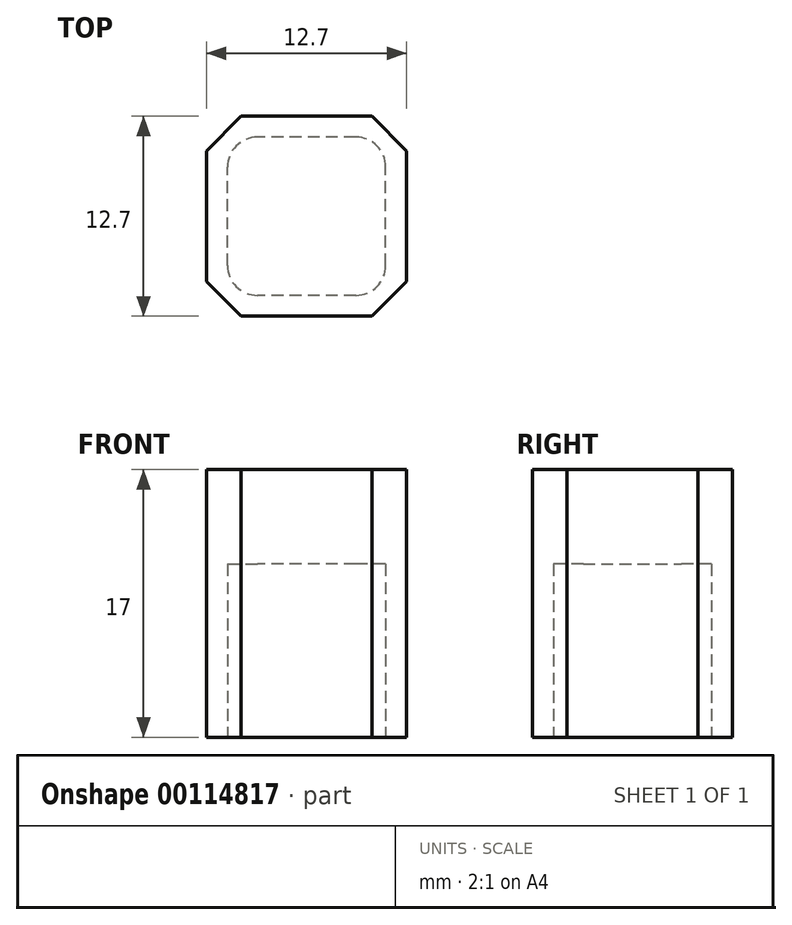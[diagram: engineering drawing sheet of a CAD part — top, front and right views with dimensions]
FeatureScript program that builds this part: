
annotation { "Feature Type Name" : "Feature", "Feature Type Description" : "" }
export const myFeature = defineFeature(function(context is Context, id is Id, definition is map)
    precondition{}
    {
        {
            var Q0;
            Q0=qCreatedBy(makeId("Top.planeOp"),FACE);
            var sketch = newSketch(context, id + "F0", { "sketchPlane" : qUnion([Q0])});
            skLineSegment(sketch, "E0.bottom", {"start": v(-30.85, -32.42) * mm, "end": v(-18.15, -32.42) * mm});
            skLineSegment(sketch, "E0.top", {"start": v(-30.85, -19.72) * mm, "end": v(-18.15, -19.72) * mm});
            skLineSegment(sketch, "E0.left", {"start": v(-30.85, -32.42) * mm, "end": v(-30.85, -19.72) * mm});
            skLineSegment(sketch, "E0.right", {"start": v(-18.15, -32.42) * mm, "end": v(-18.15, -19.72) * mm});
            skLineSegment(sketch, "E1", {"start": v(-18.15, -32.42) * mm, "end": v(-30.85, -19.72) * mm, "construction": true});
            skLineSegment(sketch, "E2", {"start": v(-30.85, -32.42) * mm, "end": v(-18.15, -19.72) * mm, "construction": true});
            skLineSegment(sketch, "E3", {"start": v(-24.5, -26.07) * mm, "end": v(-19.47, -26.07) * mm, "construction": true});
            skPoint(sketch, "E3.endSnap0", {"position": v(-24.5, -26.07) * mm});
            skLineSegment(sketch, "E4", {"start": v(-19.47, -26.07) * mm, "end": v(-19.47, -31.1) * mm, "construction": true});
            skLineSegment(sketch, "E5.bottom", {"start": v(-19.47, -31.1) * mm, "end": v(-29.52, -31.1) * mm});
            skLineSegment(sketch, "E5.top", {"start": v(-19.47, -21.05) * mm, "end": v(-29.52, -21.05) * mm});
            skLineSegment(sketch, "E5.left", {"start": v(-19.47, -31.1) * mm, "end": v(-19.47, -21.05) * mm});
            skLineSegment(sketch, "E5.right", {"start": v(-29.52, -31.1) * mm, "end": v(-29.52, -21.05) * mm});
            skSolve(sketch);
        }
        {
            var Q0;
            Q0 = qSketchRegion(id + "F0", true);
            extrude(context, id + "F1", {"entities" : qUnion([Q0]), "depth" : 17 * mm});
        }
        {
            var Q0;
            Q0=makeQuery(id+"F0.imprint","IMPRINT",FACE,{"disambiguationData":[TD([[makeQuery(id+"F0.imprint","IMPRINT",EDGE,{"derivedFrom":sQuery(id+"F0.wireOp",EDGE,"E5.bottom")}),-1.0]])]});
            extrude(context, id + "F2", {"entities" : qUnion([Q0]), "operationType" : NewBodyOperationType.ADD, "depth" : 17 * mm});
        }
        {
            var Q0;
            Q0=makeQuery(id+"F0.imprint","IMPRINT",FACE,{"disambiguationData":[TD([[makeQuery(id+"F0.imprint","IMPRINT",EDGE,{"derivedFrom":sQuery(id+"F0.wireOp",EDGE,"E5.bottom")}),-1.0]])]});
            extrude(context, id + "F3", {"entities" : qUnion([Q0]), "operationType" : NewBodyOperationType.REMOVE, "depth" : 11 * mm});
        }
        {
            var Q0;
            Q0=makeQuery(id+"F1.opExtrude","SWEPT_EDGE",EDGE,{"disambiguationData":[OSD([sQuery(id+"F0.wireOp",EDGE,"E0.top"),sQuery(id+"F0.wireOp",EDGE,"E0.right")])]});
            var Q1;
            Q1=makeQuery(id+"F1.opExtrude","SWEPT_EDGE",EDGE,{"disambiguationData":[OSD([sQuery(id+"F0.wireOp",EDGE,"E0.top"),sQuery(id+"F0.wireOp",EDGE,"E0.left")])]});
            var Q2;
            Q2=makeQuery(id+"F1.opExtrude","SWEPT_EDGE",EDGE,{"disambiguationData":[OSD([sQuery(id+"F0.wireOp",EDGE,"E0.bottom"),sQuery(id+"F0.wireOp",EDGE,"E0.left")])]});
            var Q3;
            Q3=makeQuery(id+"F1.opExtrude","SWEPT_EDGE",EDGE,{"disambiguationData":[OSD([sQuery(id+"F0.wireOp",EDGE,"E0.bottom"),sQuery(id+"F0.wireOp",EDGE,"E0.right")])]});
            chamfer(context, id + "F4", {"entities" : qUnion([Q0, Q1, Q2, Q3]), "width" : 2.2 * mm, "tangentPropagation" : true});
        }
        {
            var Q0;
            Q0=makeQuery(id+"F3.boolean.opBoolean","COPY",EDGE,{"derivedFrom":makeQuery(id+"F3.opExtrude","SWEPT_EDGE",EDGE,{"disambiguationData":[OSD([sQuery(id+"F0.wireOp",EDGE,"E5.bottom"),sQuery(id+"F0.wireOp",EDGE,"E5.left")])]})});
            var Q1;
            Q1=makeQuery(id+"F3.boolean.opBoolean","COPY",EDGE,{"derivedFrom":makeQuery(id+"F3.opExtrude","SWEPT_EDGE",EDGE,{"disambiguationData":[OSD([sQuery(id+"F0.wireOp",EDGE,"E5.top"),sQuery(id+"F0.wireOp",EDGE,"E5.left")])]})});
            var Q2;
            Q2=makeQuery(id+"F3.boolean.opBoolean","COPY",EDGE,{"derivedFrom":makeQuery(id+"F3.opExtrude","SWEPT_EDGE",EDGE,{"disambiguationData":[OSD([sQuery(id+"F0.wireOp",EDGE,"E5.top"),sQuery(id+"F0.wireOp",EDGE,"E5.right")])]})});
            var Q3;
            Q3=makeQuery(id+"F3.boolean.opBoolean","COPY",EDGE,{"derivedFrom":makeQuery(id+"F3.opExtrude","SWEPT_EDGE",EDGE,{"disambiguationData":[OSD([sQuery(id+"F0.wireOp",EDGE,"E5.bottom"),sQuery(id+"F0.wireOp",EDGE,"E5.right")])]})});
            fillet(context, id + "F5", {"entities" : qUnion([Q0, Q1, Q2, Q3]), "radius" : 1.9 * mm, "tangentPropagation" : true, "allowEdgeOverflow" : false});
        }
    });
